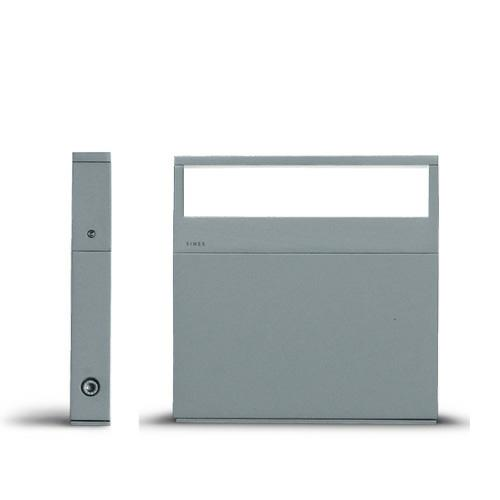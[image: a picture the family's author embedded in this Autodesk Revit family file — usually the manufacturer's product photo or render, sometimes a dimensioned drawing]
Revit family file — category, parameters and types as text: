
# Revit family: SIMES_S.7236W_Cool Bollard
name_source: partatom
category: Lighting Fixtures
revit_build: Autodesk Revit 2016 (Build: 20150714_1515(x64)
units: mm (PartAtom-declared; Revit-internal decimal feet)

## family parameters
Cut with Voids When Loaded = No
Host = Face
Light Source = Yes
OmniClass Number = 23.80.70.14
OmniClass Title = Luminaries for External Lighting
Part Type = Normal
Room Calculation Point = No
Round Connector Dimension = Use Diameter
Shared = No

## types (1)
- SIMES_S.7236W_Cool Bollard
    Approval mark = CE, ENEC
    Assembly Code = D5020
    Color Filter = 16777215
    Color Rendering Index = CRI 90
    Colour Temperature = 3000
    Control Gear = electronic transformer
    Default Elevation = 1219 mm
    Description = MINI-COOL BOLLARD H. 220mm
Art. S.7236W
MODULES LED 3000K  230V CRI 90 MacAdam step 3
Rated luminaire luminous flux: 562lm
Rated input power: 12.5W
Luminaire efficacy: 45lm/W
Electronic ballast 220÷240V 0/50/60Hz
CE - ENEC 03

PRODUCT TYPE
Bollard fitting. IP rating IP 54
MATERIAL CHARACTERISTICS
Aluminium die cast housing in EN AB-47100 (low copper content) with high resistance against corrosion. Extruded EN AW-6060 aluminium structure (bollard version) with high corrosion resistance. Stone wash surface treatment prior to painting process. A4 grade Stainless Steel screws with 2,5-3% molybdenum content which increases the resistance against corrosion. Silicone gaskets. Painting Process : 3 Step Process
1) Surface treatment with BONDERITE. A heavy metal free chemical surface treatment containing ceramic nano particles giving a cohesive, inorganic and highly dense protective coating. 2) PRE POLYMERIZATION a process of introducing an epoxy primer with excellent characteristics to the paint which also offers very high resistance to oxidation due to its Zinc content. 3) POLYMERIZATION a process with the application of polyester powder with high resistance against UV rays and harsh weather conditions. Resistance test protection for Marine applications for 1200h.  Mechanical resistance IK 06
LIGHTING PERFORMANCE
Toughened glass diffuser. LOR --. Colour rendering index  CRI 90, Colour stability step  MacAdam step 3. 
WIRING
MINI-COOL L 220m and MINI-LOOK L 220m hard wired with H07RN-F cable and fast connector IP68 included, COOL and LOOK L 290mm is supplied with single cable entry. Isolation: CLASS II . Available colours: White (cod.01), Aluminium grey (cod.14). Weight: 1.1 Kg Glow Wire test: --
Lamp included.
LOOK and COOL REGISTERED DESIGN
This luminaire contains built-in LED modules with energy class: A, A+, A++. In case of damage or malfunction please contact the manufacturer to receive additional instructions on how to replace and relative spare parts to order. The LED modules cannot be handled in the luminaire by the end user (Regulation UE 874/2012).
LED circuit boards are engineered accordingly to actual Lumen Maintenance regulation (LM80) and Technical Memorandum (TM21) where uniformity and quality of light is 50.000 hours referred to L70  B20 Ta 25°C.Lifecycle refers to LED circuit boards only, all others components of the luminaire are excluded.

EMERGENCY VERSIONS The fittings operates both on AC ( 50/60Hz ) and DC ( 0Hz ) voltage.
    Dimming Lamp Color Temperature Shift = <None>
    Frequency = 0/50/60Hz
    IFC Classification = Light Fixture
    IK Rating = IK 06
    Lamp = LED
    Lamp Light Flux = 1090
    Lamp count = 1
    Last Update = 02/08/2018 10:13:31
    Lifetime = 50000 L70 B20 Ta 25°C
    Light Output Ratio = 100
    Luminous efficacy = 45
    Manufacturer = SIMES
    Masterformat 2014 Code = 26 56 00
    Masterformat 2014 Description = Exterior Lighting
    Model = S.7236W
    Mounting Place = Floor
    Mounting Type = Surface mounted
    NBS Reference Code = 49
    NBS Reference Description = Luminaries And Lamps
    OmniClass Code = 23-35 47 11
    OmniClass Description = Lighting Fixture
    Photometric Web File = S7231W.ies
    Product Group = freestanding uplighter
    Product Name = Cool Bollard
    Protection Class = Protection class II
    Protection Degree = IP 54
    System Light Flux = 562
    System Power = 12,5
    Tilt Angle = 90.00°
    Type Comments = SIMES S.p.A. - All rights reserved
    Type Image = Cool_220.jpg
    UNSPSC Code = 3911
    URL = http://www.simes.it
    Uniclass 1.4 Code = YJ73
    Uniclass 1.4 Description = Luminaries and lamps
    Uniclass 2.0 Code = PR-49
    Uniclass 2.0 Description = Luminaries and lamps
    Uniclass 2015 Code = EF_70_80
    Uniclass 2015 Name = Lighting
    Uniformat II Code = D5020
    Uniformat II Description = Lighting & Branch Wiring
    Voltage = 220÷240V

## geometry (parser evidence)
native form markers: Sweep x3
no freeform markers — native parametric forms only
